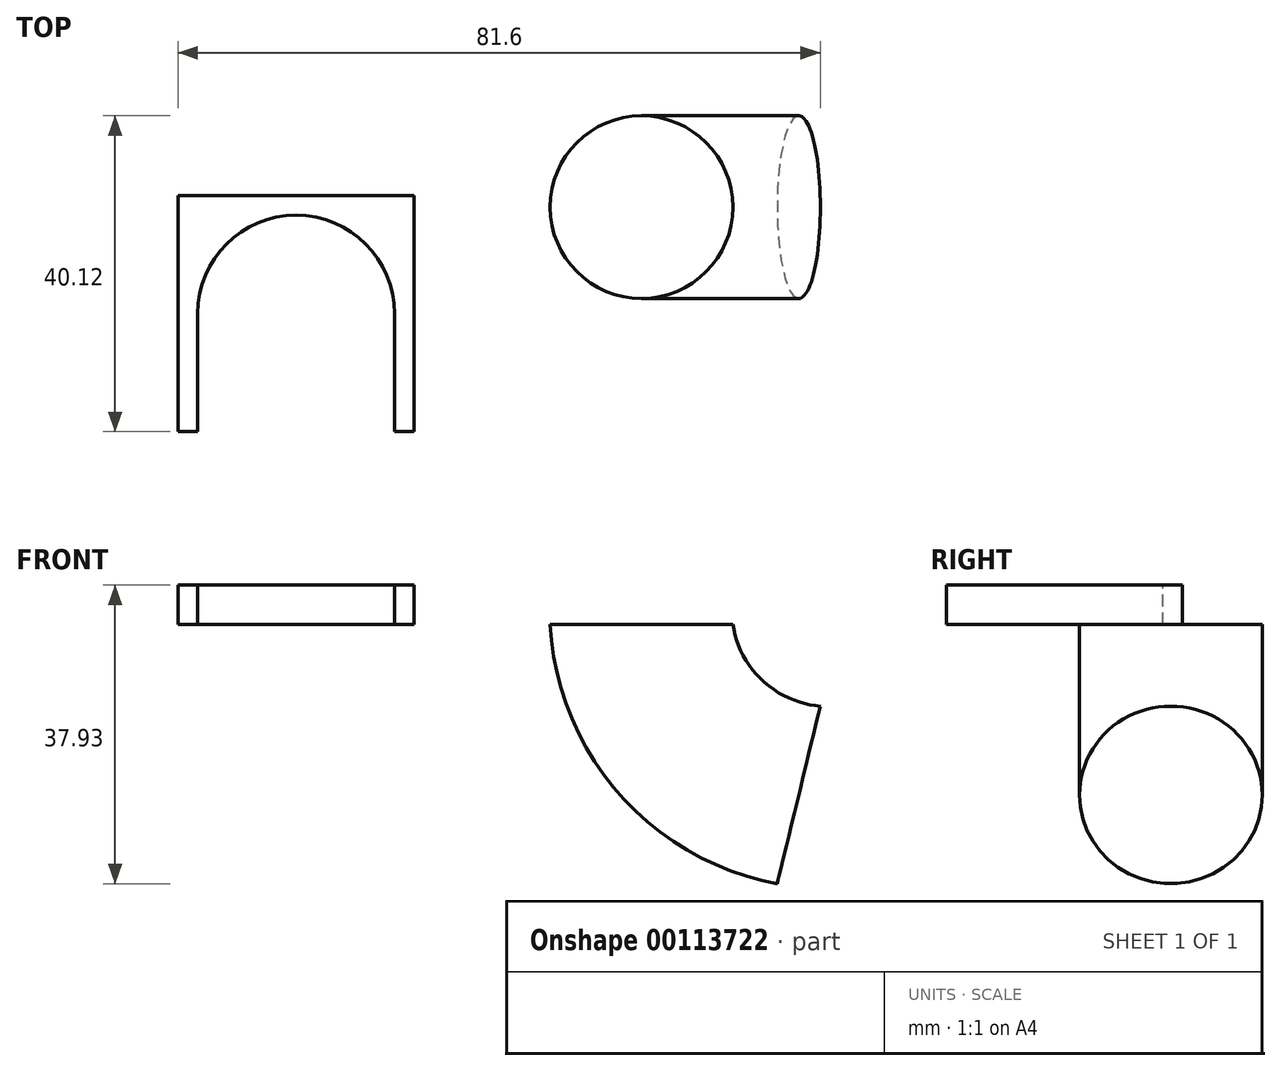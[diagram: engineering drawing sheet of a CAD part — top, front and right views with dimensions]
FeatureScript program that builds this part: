
annotation { "Feature Type Name" : "Feature", "Feature Type Description" : "" }
export const myFeature = defineFeature(function(context is Context, id is Id, definition is map)
    precondition{}
    {
        {
            var Q0;
            Q0=qCreatedBy(makeId("Top.planeOp"),FACE);
            var sketch = newSketch(context, id + "F0", { "sketchPlane" : qUnion([Q0])});
            skLineSegment(sketch, "E0.bottom", {"start": v(-15, 30) * mm, "end": v(15, 30) * mm});
            skLineSegment(sketch, "E0.top", {"start": v(-15, 0) * mm, "end": v(15, 0) * mm});
            skLineSegment(sketch, "E0.left", {"start": v(-15, 30) * mm, "end": v(-15, 0) * mm});
            skLineSegment(sketch, "E0.right", {"start": v(15, 30) * mm, "end": v(15, 0) * mm});
            skSolve(sketch);
        }
        {
            var Q0;
            Q0=makeQuery(id+"F0.imprint","IMPRINT",FACE,{"disambiguationData":[TD([[makeQuery(id+"F0.imprint","IMPRINT",EDGE,{"derivedFrom":sQuery(id+"F0.wireOp",EDGE,"E0.bottom")}),-1.0]])]});
            extrude(context, id + "F1", {"entities" : qUnion([Q0]), "depth" : 5 * mm});
        }
        {
            var Q0;
            Q0=makeQuery(id+"F1.opExtrude","CAP_FACE",FACE,{"disambiguationData":[OSD([sQuery(id+"F0.wireOp",EDGE,"E0.bottom"),sQuery(id+"F0.wireOp",EDGE,"E0.top"),sQuery(id+"F0.wireOp",EDGE,"E0.left"),sQuery(id+"F0.wireOp",EDGE,"E0.right")])],"isStart":false});
            var sketch = newSketch(context, id + "F2", { "sketchPlane" : qUnion([Q0])});
            skCircle(sketch, "E1", {"center": v(0, 15) * mm, "radius": 12.5 * mm});
            skPoint(sketch, "E1.centerSnap0", {"position": v(15, 15) * mm});
            skLineSegment(sketch, "E2", {"start": v(12.5, 15) * mm, "end": v(12.5, 0) * mm});
            skLineSegment(sketch, "E3", {"start": v(-12.5, 15) * mm, "end": v(-12.5, 0) * mm});
            skPoint(sketch, "E3.startSnap0", {"position": v(-15, 15) * mm});
            skLineSegment(sketch, "E4", {"start": v(-12.5, 0) * mm, "end": v(12.5, 0) * mm});
            skSolve(sketch);
        }
        {
            var Q0;
            {var subQ0=sQuery(id+"F2.wireOp",EDGE,"E2");Q0=makeQuery(id+"F2.imprint","IMPRINT",FACE,{"disambiguationData":[TD([[makeQuery(id+"F2.imprint","IMPRINT",EDGE,{"derivedFrom":subQ0}),-1.0]])]});}
            var Q1;
            {var subQ0=sQuery(id+"F2.wireOp",EDGE,"E1");var subQ1=makeQuery(id+"F2.imprint","INTERSECT",VERTEX,{"derivedFrom":[subQ0,sQuery(id+"F2.wireOp",EDGE,"E2")]});Q1=makeQuery(id+"F2.imprint","IMPRINT",FACE,{"disambiguationData":[TD([[makeQuery(id+"F2.imprint","IMPRINT",EDGE,{"disambiguationData":[TD([[subQ1,-1.0]])],"derivedFrom":subQ0}),1.0]])]});}
            extrude(context, id + "F3", {"entities" : qUnion([Q0, Q1]), "operationType" : NewBodyOperationType.REMOVE, "oppositeDirection" : true, "depth" : 25 * mm});
        }
        {
            var Q0;
            Q0=qCreatedBy(makeId("Top.planeOp"),FACE);
            var sketch = newSketch(context, id + "F4", { "sketchPlane" : qUnion([Q0])});
            skCircle(sketch, "E5", {"center": v(43.87, 28.51) * mm, "radius": 11.6 * mm});
            skSolve(sketch);
        }
        {
            var Q0;
            Q0=qCreatedBy(makeId("Front.planeOp"),FACE);
            var sketch = newSketch(context, id + "F5", { "sketchPlane" : qUnion([Q0])});
            skArc(sketch, "E6", {"start": v(43.87, 0) * mm, "mid": v(50.12, -14.28) * mm, "end": v(63.86, -21.66) * mm});
            skSolve(sketch);
        }
        {
            var Q0;
            Q0=makeQuery(id+"F4.imprint","IMPRINT",FACE,{"disambiguationData":[TD([[makeQuery(id+"F4.imprint","IMPRINT",EDGE,{"derivedFrom":sQuery(id+"F4.wireOp",EDGE,"E5")}),1.0]])]});
            var Q1;
            Q1=sQuery(id+"F5.wireOp",EDGE,"E6");
            sweep(context, id + "F6", {"profiles" : qUnion([Q0]), "path" : qUnion([Q1])});
        }
    });
